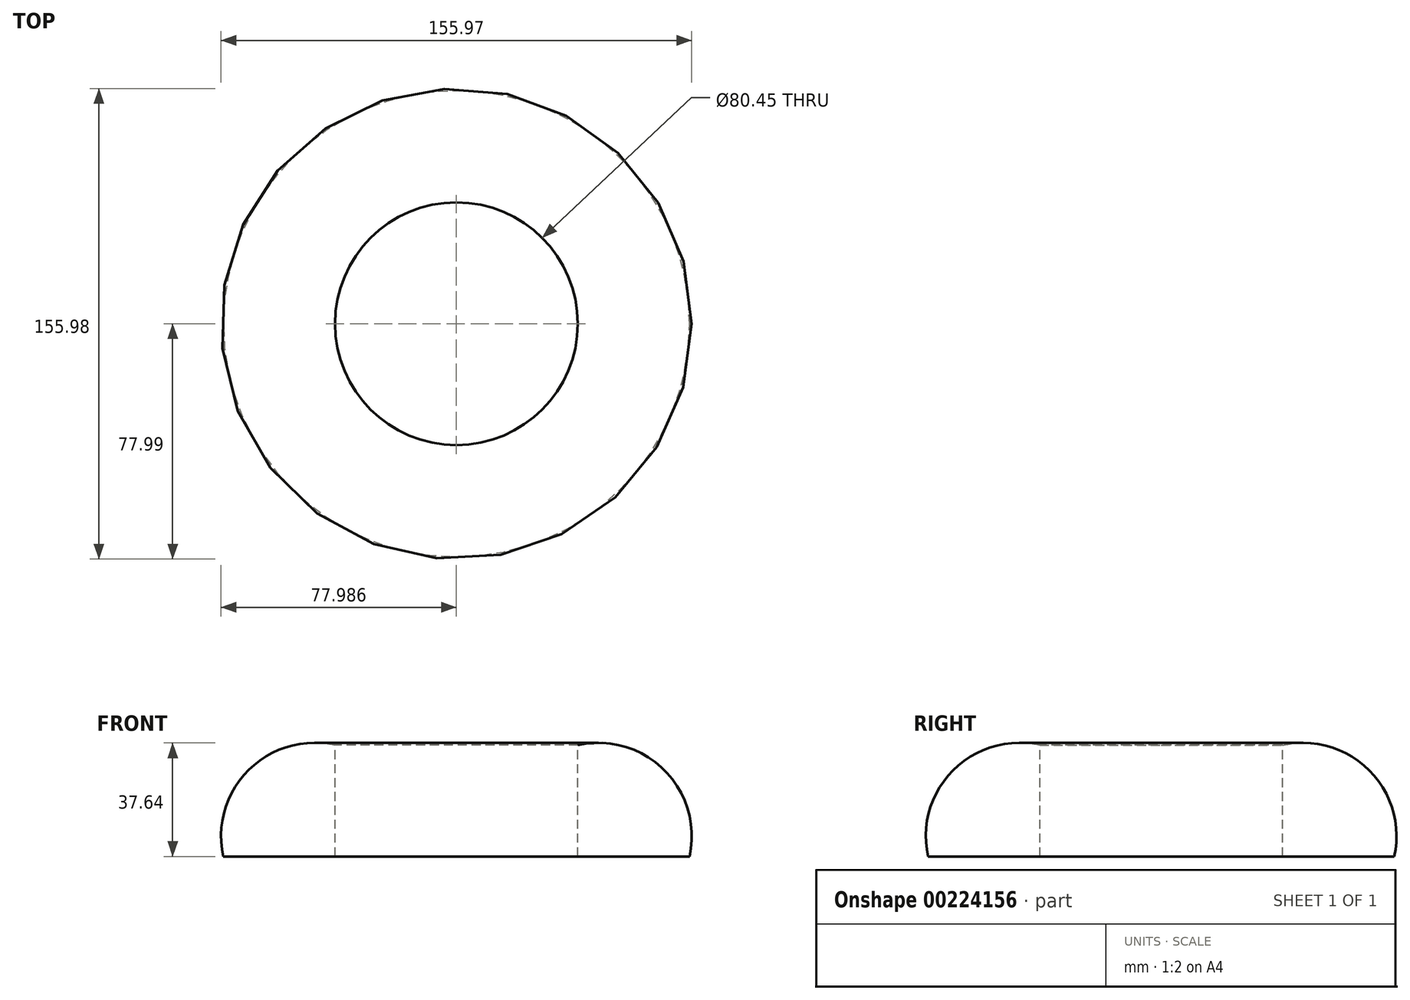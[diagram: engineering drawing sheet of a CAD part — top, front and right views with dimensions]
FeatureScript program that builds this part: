
annotation { "Feature Type Name" : "Feature", "Feature Type Description" : "" }
export const myFeature = defineFeature(function(context is Context, id is Id, definition is map)
    precondition{}
    {
        {
            var Q0;
            Q0=qCreatedBy(makeId("Front.planeOp"),FACE);
            var sketch = newSketch(context, id + "F0", { "sketchPlane" : qUnion([Q0])});
            skLineSegment(sketch, "E0", {"start": v(0, 36.87) * mm, "end": v(0, 0) * mm});
            skLineSegment(sketch, "E1", {"start": v(0, 0) * mm, "end": v(37.02, 0) * mm});
            skArc(sketch, "E2", {"start": v(37.02, 0) * mm, "mid": v(28.67, 28.63) * mm, "end": v(0, 36.87) * mm});
            skLineSegment(sketch, "E3", {"start": v(-40.22, 43.28) * mm, "end": v(-40.22, -26.38) * mm});
            skSolve(sketch);
        }
        {
            var Q0;
            Q0=makeQuery(id+"F0.imprint","IMPRINT",FACE,{"disambiguationData":[TD([[makeQuery(id+"F0.imprint","IMPRINT",EDGE,{"derivedFrom":sQuery(id+"F0.wireOp",EDGE,"E0")}),1.0]])]});
            var Q1;
            Q1=sQuery(id+"F0.wireOp",EDGE,"E3");
            revolve(context, id + "F1", {"entities" : qUnion([Q0]), "axis" : qUnion([Q1]), "revolveType" : RevolveType.FULL});
        }
    });
